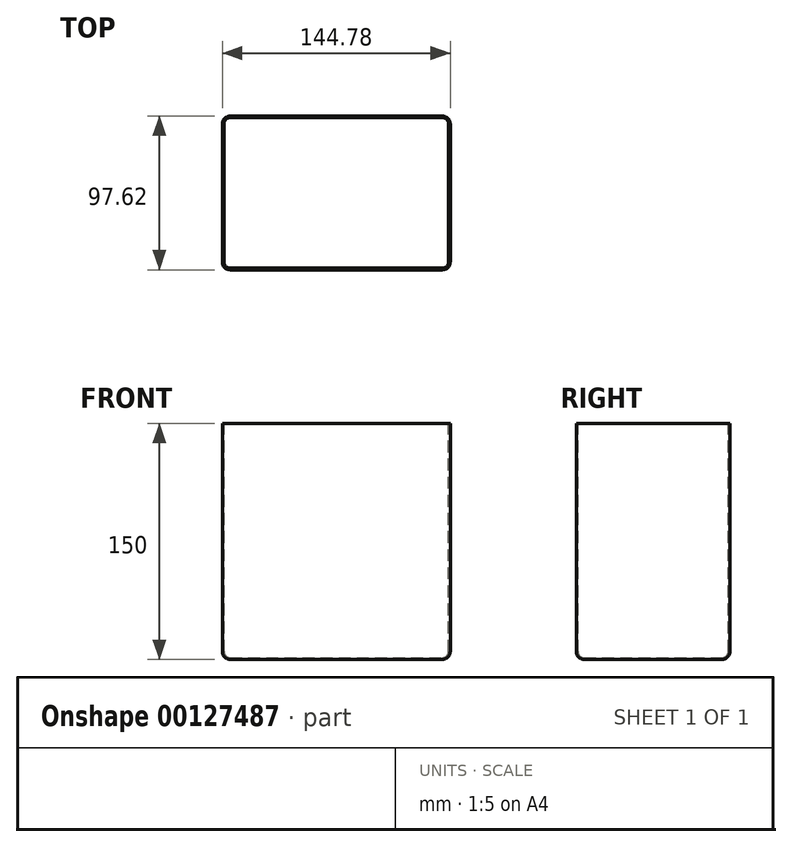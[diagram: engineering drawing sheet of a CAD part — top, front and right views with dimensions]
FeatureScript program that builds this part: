
annotation { "Feature Type Name" : "Feature", "Feature Type Description" : "" }
export const myFeature = defineFeature(function(context is Context, id is Id, definition is map)
    precondition{}
    {
        {
            var Q0;
            Q0=qCreatedBy(makeId("Top.planeOp"),FACE);
            var sketch = newSketch(context, id + "F0", { "sketchPlane" : qUnion([Q0])});
            skLineSegment(sketch, "E0.bottom", {"start": v(-72.39, -48.81) * mm, "end": v(72.39, -48.81) * mm});
            skLineSegment(sketch, "E0.top", {"start": v(-72.39, 48.81) * mm, "end": v(72.39, 48.81) * mm});
            skLineSegment(sketch, "E0.left", {"start": v(-72.39, -48.81) * mm, "end": v(-72.39, 48.81) * mm});
            skLineSegment(sketch, "E0.right", {"start": v(72.39, -48.81) * mm, "end": v(72.39, 48.81) * mm});
            skPoint(sketch, "E0.middle", {"position": v(0, 0) * mm});
            skSolve(sketch);
        }
        {
            var Q0;
            Q0=makeQuery(id+"F0.imprint","IMPRINT",FACE,{"disambiguationData":[TD([[makeQuery(id+"F0.imprint","IMPRINT",EDGE,{"derivedFrom":sQuery(id+"F0.wireOp",EDGE,"E0.bottom")}),1.0]])]});
            extrude(context, id + "F1", {"entities" : qUnion([Q0]), "depth" : 150 * mm});
        }
        {
            var Q0;
            Q0=makeQuery(id+"F1.opExtrude","CAP_FACE",FACE,{"disambiguationData":[OSD([sQuery(id+"F0.wireOp",EDGE,"E0.bottom"),sQuery(id+"F0.wireOp",EDGE,"E0.top"),sQuery(id+"F0.wireOp",EDGE,"E0.left"),sQuery(id+"F0.wireOp",EDGE,"E0.right")])],"isStart":true});
            var Q1;
            Q1=makeQuery(id+"F1.opExtrude","SWEPT_EDGE",EDGE,{"disambiguationData":[OSD([sQuery(id+"F0.wireOp",EDGE,"E0.bottom"),sQuery(id+"F0.wireOp",EDGE,"E0.left")])]});
            var Q2;
            Q2=makeQuery(id+"F1.opExtrude","SWEPT_EDGE",EDGE,{"disambiguationData":[OSD([sQuery(id+"F0.wireOp",EDGE,"E0.top"),sQuery(id+"F0.wireOp",EDGE,"E0.left")])]});
            var Q3;
            Q3=makeQuery(id+"F1.opExtrude","SWEPT_EDGE",EDGE,{"disambiguationData":[OSD([sQuery(id+"F0.wireOp",EDGE,"E0.bottom"),sQuery(id+"F0.wireOp",EDGE,"E0.right")])]});
            var Q4;
            Q4=makeQuery(id+"F1.opExtrude","SWEPT_EDGE",EDGE,{"disambiguationData":[OSD([sQuery(id+"F0.wireOp",EDGE,"E0.top"),sQuery(id+"F0.wireOp",EDGE,"E0.right")])]});
            fillet(context, id + "F2", {"entities" : qUnion([Q0, Q1, Q2, Q3, Q4]), "radius" : 5 * mm, "tangentPropagation" : true, "allowEdgeOverflow" : false});
        }
        {
            var Q0;
            Q0=makeQuery(id+"F1.opExtrude","CAP_FACE",FACE,{"disambiguationData":[OSD([sQuery(id+"F0.wireOp",EDGE,"E0.bottom"),sQuery(id+"F0.wireOp",EDGE,"E0.top"),sQuery(id+"F0.wireOp",EDGE,"E0.left"),sQuery(id+"F0.wireOp",EDGE,"E0.right")])],"isStart":false});
            shell(context, id + "F3", {"entities" : qUnion([Q0]), "thickness" : 1 * mm});
        }
    });
